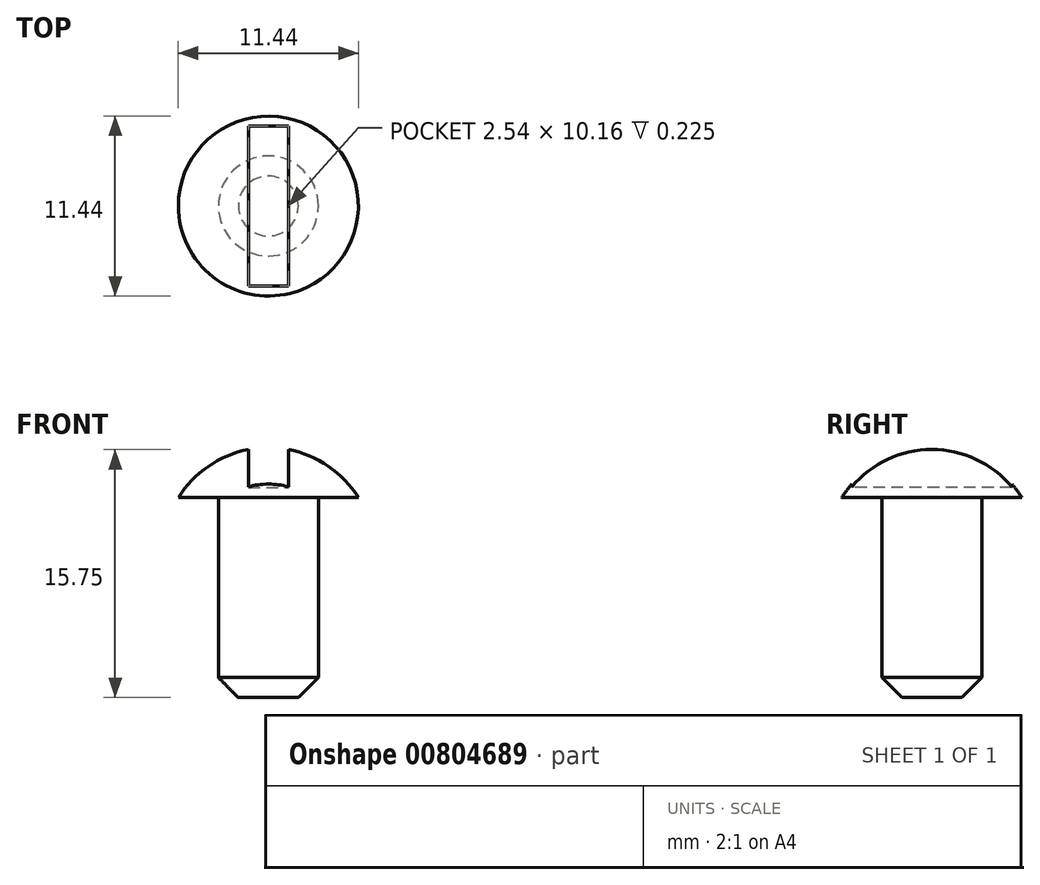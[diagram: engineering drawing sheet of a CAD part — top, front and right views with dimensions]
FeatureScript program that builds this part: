
annotation { "Feature Type Name" : "Feature", "Feature Type Description" : "" }
export const myFeature = defineFeature(function(context is Context, id is Id, definition is map)
    precondition{}
    {
        {
            var Q0;
            Q0=qCreatedBy(makeId("Front.planeOp"),FACE);
            var sketch = newSketch(context, id + "F0", { "sketchPlane" : qUnion([Q0])});
            skLineSegment(sketch, "E0", {"start": v(0, 0) * mm, "end": v(0, 17.88) * mm, "construction": true});
            skLineSegment(sketch, "E1", {"start": v(0, 0) * mm, "end": v(3.18, 0) * mm});
            skLineSegment(sketch, "E2", {"start": v(3.18, 0) * mm, "end": v(3.18, 12.7) * mm});
            skLineSegment(sketch, "E3", {"start": v(3.18, 12.7) * mm, "end": v(5.72, 12.7) * mm});
            skLineSegment(sketch, "E4", {"start": v(5.72, 12.7) * mm, "end": v(5.72, 15.88) * mm, "construction": true});
            skArc(sketch, "E5", {"start": v(5.72, 12.7) * mm, "mid": v(3.27, 15.03) * mm, "end": v(0, 15.88) * mm});
            skLineSegment(sketch, "E6", {"start": v(0, 15.88) * mm, "end": v(0, 0) * mm});
            skSolve(sketch);
        }
        {
            var Q0;
            Q0=makeQuery(id+"F0.imprint","IMPRINT",FACE,{"disambiguationData":[TD([[makeQuery(id+"F0.imprint","IMPRINT",EDGE,{"derivedFrom":sQuery(id+"F0.wireOp",EDGE,"E1")}),1.0]])]});
            var Q1;
            Q1=sQuery(id+"F0.wireOp",EDGE,"E0");
            revolve(context, id + "F1", {"surfaceOperationType" : NewSurfaceOperationType.NEW, "entities" : qUnion([Q0]), "axis" : qUnion([Q1]), "revolveType" : RevolveType.FULL});
        }
        {
            var Q0;
            Q0=makeQuery(id+"F1.opRevolve","SWEPT_FACE",FACE,{"disambiguationData":[OSD([sQuery(id+"F0.wireOp",EDGE,"E3")])]});
            cPlane(context, id + "F2", {"entities" : qUnion([Q0]), "cplaneType" : CPlaneType.OFFSET, "offset" : 0.64 * mm, "oppositeDirection" : true, "width" : 152.4 * mm, "height" : 152.4 * mm});
        }
        {
            var Q0;
            Q0=qCreatedBy(id+"F2.planeOp",FACE);
            var sketch = newSketch(context, id + "F3", { "sketchPlane" : qUnion([Q0])});
            skLineSegment(sketch, "E7.bottom", {"start": v(-1.27, -5.08) * mm, "end": v(1.27, -5.08) * mm});
            skLineSegment(sketch, "E7.top", {"start": v(-1.27, 5.08) * mm, "end": v(1.27, 5.08) * mm});
            skLineSegment(sketch, "E7.left", {"start": v(-1.27, -5.08) * mm, "end": v(-1.27, 5.08) * mm});
            skLineSegment(sketch, "E7.right", {"start": v(1.27, -5.08) * mm, "end": v(1.27, 5.08) * mm});
            skSolve(sketch);
        }
        {
            var Q0;
            Q0 = qSketchRegion(id + "F3", true);
            extrude(context, id + "F4", {"entities" : qUnion([Q0]), "operationType" : NewBodyOperationType.REMOVE, "endBound" : BoundingType.THROUGH_ALL, "oppositeDirection" : true, "depth" : 25.4 * mm, "offsetDistance" : 25.4 * mm});
        }
        {
            var Q0;
            Q0=makeQuery(id+"F1.opRevolve","SWEPT_EDGE",EDGE,{"disambiguationData":[OSD([sQuery(id+"F0.wireOp",EDGE,"E1"),sQuery(id+"F0.wireOp",EDGE,"E2")])]});
            chamfer(context, id + "F5", {"entities" : qUnion([Q0]), "width" : 1.27 * mm, "tangentPropagation" : true});
        }
    });
